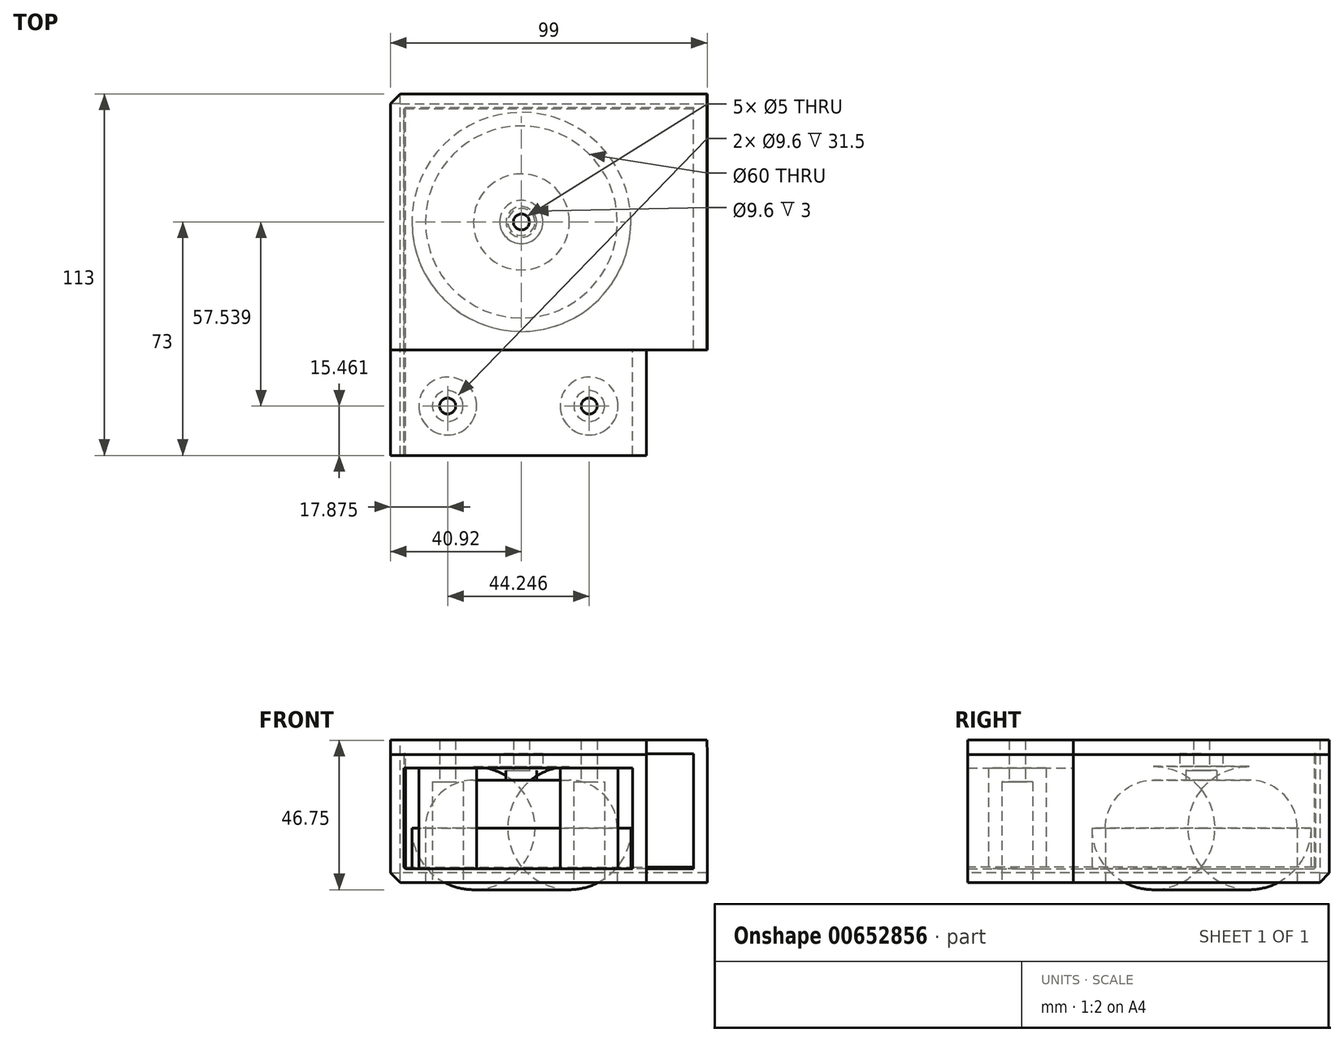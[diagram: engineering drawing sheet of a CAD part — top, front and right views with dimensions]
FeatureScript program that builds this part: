
annotation { "Feature Type Name" : "Feature", "Feature Type Description" : "" }
export const myFeature = defineFeature(function(context is Context, id is Id, definition is map)
    precondition{}
    {
        {
            var Q0;
            Q0=qCreatedBy(makeId("Front.planeOp"),FACE);
            var sketch = newSketch(context, id + "F0", { "sketchPlane" : qUnion([Q0])});
            skLineSegment(sketch, "E0.bottom", {"start": v(-40.92, -8.88) * mm, "end": v(39.08, -8.88) * mm});
            skLineSegment(sketch, "E0.top", {"start": v(-40.92, 31.12) * mm, "end": v(39.08, 31.12) * mm});
            skLineSegment(sketch, "E0.left", {"start": v(-40.92, -8.88) * mm, "end": v(-40.92, 31.12) * mm});
            skLineSegment(sketch, "E0.right", {"start": v(39.08, -8.88) * mm, "end": v(39.08, 31.12) * mm});
            skLineSegment(sketch, "E1.0", {"start": v(-40.92, 35.62) * mm, "end": v(39.08, 35.62) * mm});
            skLineSegment(sketch, "E2.0", {"start": v(58.08, -8.88) * mm, "end": v(58.08, 31.12) * mm});
            skLineSegment(sketch, "E3", {"start": v(-40.92, 35.62) * mm, "end": v(-40.92, 31.12) * mm});
            skLineSegment(sketch, "E4", {"start": v(39.08, 35.62) * mm, "end": v(39.08, 31.12) * mm});
            skLineSegment(sketch, "E5", {"start": v(39.08, 35.62) * mm, "end": v(58, 35.62) * mm});
            skLineSegment(sketch, "E6", {"start": v(58, 35.62) * mm, "end": v(58.08, 31.12) * mm});
            skLineSegment(sketch, "E7", {"start": v(58.08, -8.88) * mm, "end": v(39.08, -8.88) * mm});
            skSolve(sketch);
        }
        {
            var Q0;
            Q0=makeQuery(id+"F0.imprint","IMPRINT",FACE,{"disambiguationData":[TD([[makeQuery(id+"F0.imprint","IMPRINT",EDGE,{"derivedFrom":sQuery(id+"F0.wireOp",EDGE,"E0.bottom")}),1.0]])]});
            extrude(context, id + "F1", {"entities" : qUnion([Q0]), "depth" : 113 * mm, "offsetDistance" : 25 * mm});
        }
        {
            var Q0;
            Q0=makeQuery(id+"F0.imprint","IMPRINT",FACE,{"disambiguationData":[TD([[makeQuery(id+"F0.imprint","IMPRINT",EDGE,{"derivedFrom":sQuery(id+"F0.wireOp",EDGE,"E0.top")}),1.0]])]});
            var Q1;
            Q1=makeQuery(id+"F0.imprint","IMPRINT",FACE,{"disambiguationData":[TD([[makeQuery(id+"F0.imprint","IMPRINT",EDGE,{"derivedFrom":sQuery(id+"F0.wireOp",EDGE,"E0.right")}),-1.0]])]});
            extrude(context, id + "F2", {"entities" : qUnion([Q0, Q1]), "operationType" : NewBodyOperationType.ADD, "depth" : 80 * mm, "offsetDistance" : 25 * mm});
        }
        {
            var Q0;
            Q0=makeQuery(id+"F2.boolean.opBoolean","MERGE",FACE,{"derivedFrom":[makeQuery(id+"F1.opExtrude","SWEPT_FACE",FACE,{"disambiguationData":[OSD([sQuery(id+"F0.wireOp",EDGE,"E0.bottom")])]}),makeQuery(id+"F2.opExtrude","SWEPT_FACE",FACE,{"disambiguationData":[OSD([sQuery(id+"F0.wireOp",EDGE,"E7")])]})]});
            var sketch = newSketch(context, id + "F3", { "sketchPlane" : qUnion([Q0])});
            skCircle(sketch, "E8", {"center": v(0, 40) * mm, "radius": 30 * mm});
            skSolve(sketch);
        }
        {
            var Q0;
            Q0=makeQuery(id+"F3.imprint","IMPRINT",FACE,{"disambiguationData":[TD([[makeQuery(id+"F3.imprint","IMPRINT",EDGE,{"derivedFrom":sQuery(id+"F3.wireOp",EDGE,"E8")}),1.0]])]});
            extrude(context, id + "F4", {"entities" : qUnion([Q0]), "operationType" : NewBodyOperationType.REMOVE, "oppositeDirection" : true, "depth" : 32 * mm, "offsetDistance" : 25 * mm});
        }
        {
            var Q0;
            Q0=makeQuery(id+"F2.boolean.opBoolean","MERGE",FACE,{"derivedFrom":[makeQuery(id+"F1.opExtrude","SWEPT_FACE",FACE,{"disambiguationData":[OSD([sQuery(id+"F0.wireOp",EDGE,"E0.bottom")])]}),makeQuery(id+"F2.opExtrude","SWEPT_FACE",FACE,{"disambiguationData":[OSD([sQuery(id+"F0.wireOp",EDGE,"E7")])]})]});
            var sketch = newSketch(context, id + "F5", { "sketchPlane" : qUnion([Q0])});
            skCircle(sketch, "E9", {"center": v(-23.04, 97.54) * mm, "radius": 2.5 * mm});
            skCircle(sketch, "E10", {"center": v(21.2, 97.54) * mm, "radius": 2.5 * mm});
            skCircle(sketch, "E11", {"center": v(0, 40) * mm, "radius": 2.5 * mm});
            skCircle(sketch, "E12.0", {"center": v(21.2, 97.54) * mm, "radius": 4.8 * mm});
            skCircle(sketch, "E13.0", {"center": v(-23.04, 97.54) * mm, "radius": 4.8 * mm});
            skCircle(sketch, "E14.0", {"center": v(0, 40) * mm, "radius": 4.8 * mm});
            skSolve(sketch);
        }
        {
            var Q0;
            Q0=makeQuery(id+"F5.imprint","IMPRINT",FACE,{"disambiguationData":[TD([[makeQuery(id+"F5.imprint","IMPRINT",EDGE,{"derivedFrom":sQuery(id+"F5.wireOp",EDGE,"E9")}),1.0]])]});
            var Q1;
            Q1=makeQuery(id+"F5.imprint","IMPRINT",FACE,{"disambiguationData":[TD([[makeQuery(id+"F5.imprint","IMPRINT",EDGE,{"derivedFrom":sQuery(id+"F5.wireOp",EDGE,"E10")}),1.0]])]});
            var Q2;
            Q2=makeQuery(id+"F5.imprint","IMPRINT",FACE,{"disambiguationData":[TD([[makeQuery(id+"F5.imprint","IMPRINT",EDGE,{"derivedFrom":sQuery(id+"F5.wireOp",EDGE,"E11")}),1.0]])]});
            extrude(context, id + "F6", {"entities" : qUnion([Q0, Q1, Q2]), "operationType" : NewBodyOperationType.REMOVE, "endBound" : BoundingType.THROUGH_ALL, "oppositeDirection" : true, "depth" : 25 * mm, "offsetDistance" : 25 * mm});
        }
        {
            var Q0;
            Q0=makeQuery(id+"F4.boolean.opBoolean","COPY",EDGE,{"derivedFrom":makeQuery(id+"F4.opExtrude","CAP_EDGE",EDGE,{"disambiguationData":[OSD([sQuery(id+"F3.wireOp",EDGE,"E8")])],"isStart":false})});
            fillet(context, id + "F7", {"entities" : qUnion([Q0]), "radius" : 15 * mm, "tangentPropagation" : true, "allowEdgeOverflow" : false});
        }
        {
            var Q0;
            Q0=makeQuery(id+"F4.boolean.opBoolean","COPY",EDGE,{"derivedFrom":makeQuery(id+"F4.opExtrude","CAP_EDGE",EDGE,{"disambiguationData":[OSD([sQuery(id+"F3.wireOp",EDGE,"E8")])],"isStart":true})});
            var Q1;
            Q1=makeQuery(id+"F1.opExtrude","SWEPT_EDGE",EDGE,{"disambiguationData":[OSD([sQuery(id+"F0.wireOp",EDGE,"E0.bottom"),sQuery(id+"F0.wireOp",EDGE,"E0.left")])]});
            var Q2;
            Q2=makeQuery(id+"F2.boolean.opBoolean","MERGE",EDGE,{"derivedFrom":[makeQuery(id+"F1.opExtrude","CAP_EDGE",EDGE,{"disambiguationData":[OSD([sQuery(id+"F0.wireOp",EDGE,"E0.left")])],"isStart":true}),makeQuery(id+"F2.opExtrude","CAP_EDGE",EDGE,{"disambiguationData":[OSD([sQuery(id+"F0.wireOp",EDGE,"E3")])],"isStart":true})]});
            var Q3;
            Q3=makeQuery(id+"F2.boolean.opBoolean","MERGE",EDGE,{"derivedFrom":[makeQuery(id+"F1.opExtrude","CAP_EDGE",EDGE,{"disambiguationData":[OSD([sQuery(id+"F0.wireOp",EDGE,"E0.bottom")])],"isStart":true}),makeQuery(id+"F2.opExtrude","CAP_EDGE",EDGE,{"disambiguationData":[OSD([sQuery(id+"F0.wireOp",EDGE,"E7")])],"isStart":true})]});
            var Q4;
            Q4=makeQuery(id+"F6.boolean.opBoolean","COPY",EDGE,{"derivedFrom":makeQuery(id+"F6.opExtrude","CAP_EDGE",EDGE,{"disambiguationData":[OSD([sQuery(id+"F5.wireOp",EDGE,"E10")])],"isStart":true})});
            var Q5;
            Q5=makeQuery(id+"F6.boolean.opBoolean","COPY",EDGE,{"derivedFrom":makeQuery(id+"F6.opExtrude","CAP_EDGE",EDGE,{"disambiguationData":[OSD([sQuery(id+"F5.wireOp",EDGE,"E9")])],"isStart":true})});
            chamfer(context, id + "F8", {"entities" : qUnion([Q0, Q1, Q2, Q3, Q4, Q5]), "width" : 3 * mm, "tangentPropagation" : true});
        }
        {
            var Q0;
            Q0=makeQuery(id+"F5.imprint","IMPRINT",FACE,{"disambiguationData":[TD([[makeQuery(id+"F5.imprint","IMPRINT",EDGE,{"derivedFrom":sQuery(id+"F5.wireOp",EDGE,"E10")}),-1.0]])]});
            var Q1;
            Q1=makeQuery(id+"F5.imprint","IMPRINT",FACE,{"disambiguationData":[TD([[makeQuery(id+"F5.imprint","IMPRINT",EDGE,{"derivedFrom":sQuery(id+"F5.wireOp",EDGE,"E9")}),-1.0]])]});
            extrude(context, id + "F9", {"entities" : qUnion([Q0, Q1]), "operationType" : NewBodyOperationType.REMOVE, "oppositeDirection" : true, "depth" : 31.5 * mm, "offsetDistance" : 25 * mm});
        }
        {
            var Q0;
            Q0=makeQuery(id+"F1.opExtrude","CAP_FACE",FACE,{"disambiguationData":[OSD([sQuery(id+"F0.wireOp",EDGE,"E0.bottom"),sQuery(id+"F0.wireOp",EDGE,"E0.top"),sQuery(id+"F0.wireOp",EDGE,"E0.left"),sQuery(id+"F0.wireOp",EDGE,"E0.right")])],"isStart":false});
            var Q1;
            Q1=makeQuery(id+"F2.opExtrude","CAP_FACE",FACE,{"disambiguationData":[OSD([sQuery(id+"F0.wireOp",EDGE,"E0.top"),sQuery(id+"F0.wireOp",EDGE,"E0.right"),sQuery(id+"F0.wireOp",EDGE,"E1.0"),sQuery(id+"F0.wireOp",EDGE,"E2.0"),sQuery(id+"F0.wireOp",EDGE,"E3"),sQuery(id+"F0.wireOp",EDGE,"E5"),sQuery(id+"F0.wireOp",EDGE,"E6"),sQuery(id+"F0.wireOp",EDGE,"E7")])],"isStart":false});
            shell(context, id + "F10", {"entities" : qUnion([Q0, Q1]), "thickness" : 4.25 * mm});
        }
        {
            var Q0;
            Q0=makeQuery(id+"F1.opExtrude","SWEPT_FACE",FACE,{"disambiguationData":[OSD([sQuery(id+"F0.wireOp",EDGE,"E0.top")])]});
            extrude(context, id + "F11", {"entities" : qUnion([Q0]), "depth" : 4.5 * mm, "offsetDistance" : 25 * mm});
        }
        {
            var Q0;
            Q0=makeQuery(id+"F5.imprint","IMPRINT",FACE,{"disambiguationData":[TD([[makeQuery(id+"F5.imprint","IMPRINT",EDGE,{"derivedFrom":sQuery(id+"F5.wireOp",EDGE,"E11")}),-1.0]])]});
            extrude(context, id + "F12", {"entities" : qUnion([Q0]), "operationType" : NewBodyOperationType.REMOVE, "oppositeDirection" : true, "depth" : 35 * mm, "offsetDistance" : 25 * mm});
        }
    });
